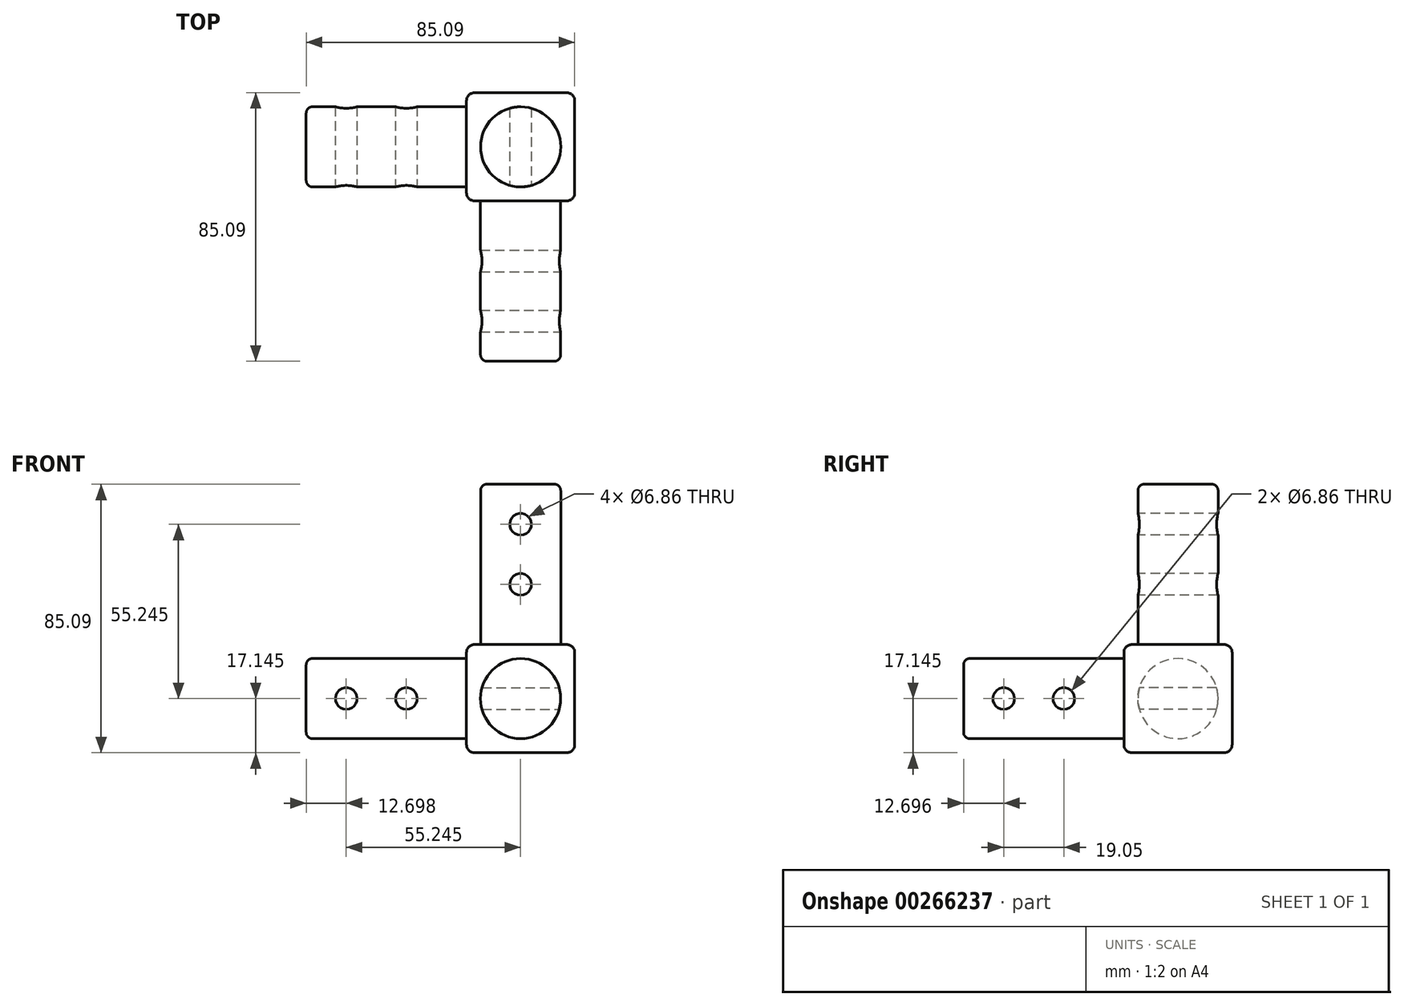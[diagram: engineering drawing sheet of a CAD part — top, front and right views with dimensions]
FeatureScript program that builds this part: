
annotation { "Feature Type Name" : "Feature", "Feature Type Description" : "" }
export const myFeature = defineFeature(function(context is Context, id is Id, definition is map)
    precondition{}
    {
        {
            var Q0;
            Q0=qCreatedBy(makeId("Top.planeOp"),FACE);
            var sketch = newSketch(context, id + "F0", { "sketchPlane" : qUnion([Q0])});
            skLineSegment(sketch, "E0.bottom", {"start": v(-13.47, 23.7) * mm, "end": v(20.82, 23.7) * mm});
            skLineSegment(sketch, "E0.top", {"start": v(-13.47, -10.58) * mm, "end": v(20.82, -10.58) * mm});
            skLineSegment(sketch, "E0.left", {"start": v(-13.47, 23.7) * mm, "end": v(-13.47, -10.58) * mm});
            skLineSegment(sketch, "E0.right", {"start": v(20.82, 23.7) * mm, "end": v(20.82, -10.58) * mm});
            skSolve(sketch);
        }
        {
            var Q0;
            Q0=qSketchRegion(id+"F0",true);
            extrude(context, id + "F1", {"entities" : qUnion([Q0]), "depth" : 34.3 * mm});
        }
        {
            var Q0;
            Q0=makeQuery(id+"F1.opExtrude","CAP_FACE",FACE,{"disambiguationData":[OSD([sQuery(id+"F0.wireOp",EDGE,"E0.bottom"),sQuery(id+"F0.wireOp",EDGE,"E0.top"),sQuery(id+"F0.wireOp",EDGE,"E0.left"),sQuery(id+"F0.wireOp",EDGE,"E0.right")])],"isStart":false});
            var sketch = newSketch(context, id + "F2", { "sketchPlane" : qUnion([Q0])});
            skCircle(sketch, "E1", {"center": v(3.68, 6.56) * mm, "radius": 12.7 * mm});
            skLineSegment(sketch, "E2", {"start": v(3.67, 23.7) * mm, "end": v(3.67, -12.79) * mm, "construction": true});
            skLineSegment(sketch, "E3", {"start": v(20.82, 6.56) * mm, "end": v(-13.47, 6.56) * mm, "construction": true});
            skSolve(sketch);
        }
        {
            var Q0;
            Q0=qSketchRegion(id+"F2",true);
            extrude(context, id + "F3", {"entities" : qUnion([Q0]), "operationType" : NewBodyOperationType.ADD, "depth" : 50.8 * mm});
        }
        {
            var Q0;
            Q0=makeQuery(id+"F1.opExtrude","SWEPT_FACE",FACE,{"disambiguationData":[OSD([sQuery(id+"F0.wireOp",EDGE,"E0.left")])]});
            var sketch = newSketch(context, id + "F4", { "sketchPlane" : qUnion([Q0])});
            skLineSegment(sketch, "E4", {"start": v(-23.7, 17.15) * mm, "end": v(13.45, 17.15) * mm, "construction": true});
            skLineSegment(sketch, "E5", {"start": v(-6.56, 0) * mm, "end": v(-6.56, 34.3) * mm, "construction": true});
            skCircle(sketch, "E6", {"center": v(-6.56, 17.15) * mm, "radius": 12.7 * mm});
            skSolve(sketch);
        }
        {
            var Q0;
            Q0=qSketchRegion(id+"F4",true);
            extrude(context, id + "F5", {"entities" : qUnion([Q0]), "operationType" : NewBodyOperationType.ADD, "depth" : 50.8 * mm});
        }
        {
            var Q0;
            Q0=makeQuery(id+"F1.opExtrude","SWEPT_FACE",FACE,{"disambiguationData":[OSD([sQuery(id+"F0.wireOp",EDGE,"E0.top")])]});
            var sketch = newSketch(context, id + "F6", { "sketchPlane" : qUnion([Q0])});
            skLineSegment(sketch, "E7", {"start": v(-13.47, 17.15) * mm, "end": v(24.43, 17.15) * mm, "construction": true});
            skLineSegment(sketch, "E8", {"start": v(3.67, 0) * mm, "end": v(3.67, 34.3) * mm, "construction": true});
            skCircle(sketch, "E9", {"center": v(3.67, 17.15) * mm, "radius": 12.7 * mm});
            skSolve(sketch);
        }
        {
            var Q0;
            Q0=qSketchRegion(id+"F6",true);
            extrude(context, id + "F7", {"entities" : qUnion([Q0]), "operationType" : NewBodyOperationType.ADD, "depth" : 50.8 * mm});
        }
        {
            var Q0;
            Q0=qCreatedBy(makeId("Front.planeOp"),FACE);
            var sketch = newSketch(context, id + "F8", { "sketchPlane" : qUnion([Q0])});
            skCircle(sketch, "E10", {"center": v(3.67, 53.34) * mm, "radius": 3.43 * mm});
            skCircle(sketch, "E11", {"center": v(3.67, 72.4) * mm, "radius": 3.43 * mm});
            skSolve(sketch);
        }
        {
            var Q0;
            Q0=qSketchRegion(id+"F8",true);
            extrude(context, id + "F9", {"entities" : qUnion([Q0]), "operationType" : NewBodyOperationType.REMOVE, "endBound" : BoundingType.SYMMETRIC, "oppositeDirection" : true, "depth" : 50.8 * mm});
        }
        {
            var Q0;
            Q0=qCreatedBy(makeId("Right.planeOp"),FACE);
            var sketch = newSketch(context, id + "F10", { "sketchPlane" : qUnion([Q0])});
            skCircle(sketch, "E12", {"center": v(-29.63, 17.15) * mm, "radius": 3.43 * mm});
            skCircle(sketch, "E13", {"center": v(-48.68, 17.15) * mm, "radius": 3.43 * mm});
            skSolve(sketch);
        }
        {
            var Q0;
            Q0=qSketchRegion(id+"F10",true);
            extrude(context, id + "F11", {"entities" : qUnion([Q0]), "operationType" : NewBodyOperationType.REMOVE, "endBound" : BoundingType.SYMMETRIC, "oppositeDirection" : true, "depth" : 50.8 * mm});
        }
        {
            var Q0;
            Q0=qCreatedBy(makeId("Front.planeOp"),FACE);
            var sketch = newSketch(context, id + "F12", { "sketchPlane" : qUnion([Q0])});
            skCircle(sketch, "E14", {"center": v(-51.57, 17.15) * mm, "radius": 3.43 * mm});
            skCircle(sketch, "E15", {"center": v(-32.52, 17.15) * mm, "radius": 3.43 * mm});
            skSolve(sketch);
        }
        {
            var Q0;
            Q0=qSketchRegion(id+"F12",true);
            extrude(context, id + "F13", {"entities" : qUnion([Q0]), "operationType" : NewBodyOperationType.REMOVE, "endBound" : BoundingType.SYMMETRIC, "oppositeDirection" : true, "depth" : 50.8 * mm});
        }
        {
            var Q0;
            Q0=makeQuery(id+"F3.opExtrude","CAP_EDGE",EDGE,{"disambiguationData":[OSD([sQuery(id+"F2.wireOp",EDGE,"E1")])],"isStart":false});
            var Q1;
            Q1=makeQuery(id+"F7.opExtrude","CAP_EDGE",EDGE,{"disambiguationData":[OSD([sQuery(id+"F6.wireOp",EDGE,"E9")])],"isStart":false});
            var Q2;
            Q2=makeQuery(id+"F5.opExtrude","CAP_EDGE",EDGE,{"disambiguationData":[OSD([sQuery(id+"F4.wireOp",EDGE,"E6")])],"isStart":false});
            fillet(context, id + "F14", {"entities" : qUnion([Q0, Q1, Q2]), "radius" : 2.03 * mm, "tangentPropagation" : true, "allowEdgeOverflow" : false});
        }
        {
            var Q0;
            Q0=makeQuery(id+"F1.opExtrude","SWEPT_EDGE",EDGE,{"disambiguationData":[OSD([sQuery(id+"F0.wireOp",EDGE,"E0.bottom"),sQuery(id+"F0.wireOp",EDGE,"E0.right")])]});
            var Q1;
            Q1=makeQuery(id+"F1.opExtrude","CAP_EDGE",EDGE,{"disambiguationData":[OSD([sQuery(id+"F0.wireOp",EDGE,"E0.right")])],"isStart":false});
            var Q2;
            Q2=makeQuery(id+"F1.opExtrude","SWEPT_EDGE",EDGE,{"disambiguationData":[OSD([sQuery(id+"F0.wireOp",EDGE,"E0.top"),sQuery(id+"F0.wireOp",EDGE,"E0.right")])]});
            var Q3;
            Q3=makeQuery(id+"F1.opExtrude","CAP_EDGE",EDGE,{"disambiguationData":[OSD([sQuery(id+"F0.wireOp",EDGE,"E0.right")])],"isStart":true});
            var Q4;
            Q4=makeQuery(id+"F1.opExtrude","CAP_EDGE",EDGE,{"disambiguationData":[OSD([sQuery(id+"F0.wireOp",EDGE,"E0.bottom")])],"isStart":true});
            var Q5;
            Q5=makeQuery(id+"F1.opExtrude","CAP_EDGE",EDGE,{"disambiguationData":[OSD([sQuery(id+"F0.wireOp",EDGE,"E0.bottom")])],"isStart":false});
            var Q6;
            Q6=makeQuery(id+"F1.opExtrude","SWEPT_EDGE",EDGE,{"disambiguationData":[OSD([sQuery(id+"F0.wireOp",EDGE,"E0.bottom"),sQuery(id+"F0.wireOp",EDGE,"E0.left")])]});
            var Q7;
            Q7=makeQuery(id+"F1.opExtrude","CAP_EDGE",EDGE,{"disambiguationData":[OSD([sQuery(id+"F0.wireOp",EDGE,"E0.left")])],"isStart":true});
            var Q8;
            Q8=makeQuery(id+"F1.opExtrude","CAP_EDGE",EDGE,{"disambiguationData":[OSD([sQuery(id+"F0.wireOp",EDGE,"E0.top")])],"isStart":true});
            var Q9;
            Q9=makeQuery(id+"F1.opExtrude","CAP_EDGE",EDGE,{"disambiguationData":[OSD([sQuery(id+"F0.wireOp",EDGE,"E0.left")])],"isStart":false});
            var Q10;
            Q10=makeQuery(id+"F1.opExtrude","SWEPT_EDGE",EDGE,{"disambiguationData":[OSD([sQuery(id+"F0.wireOp",EDGE,"E0.top"),sQuery(id+"F0.wireOp",EDGE,"E0.left")])]});
            var Q11;
            Q11=makeQuery(id+"F1.opExtrude","CAP_EDGE",EDGE,{"disambiguationData":[OSD([sQuery(id+"F0.wireOp",EDGE,"E0.top")])],"isStart":false});
            fillet(context, id + "F15", {"entities" : qUnion([Q0, Q1, Q2, Q3, Q4, Q5, Q6, Q7, Q8, Q9, Q10, Q11]), "radius" : 2.54 * mm, "tangentPropagation" : true, "allowEdgeOverflow" : false});
        }
    });
